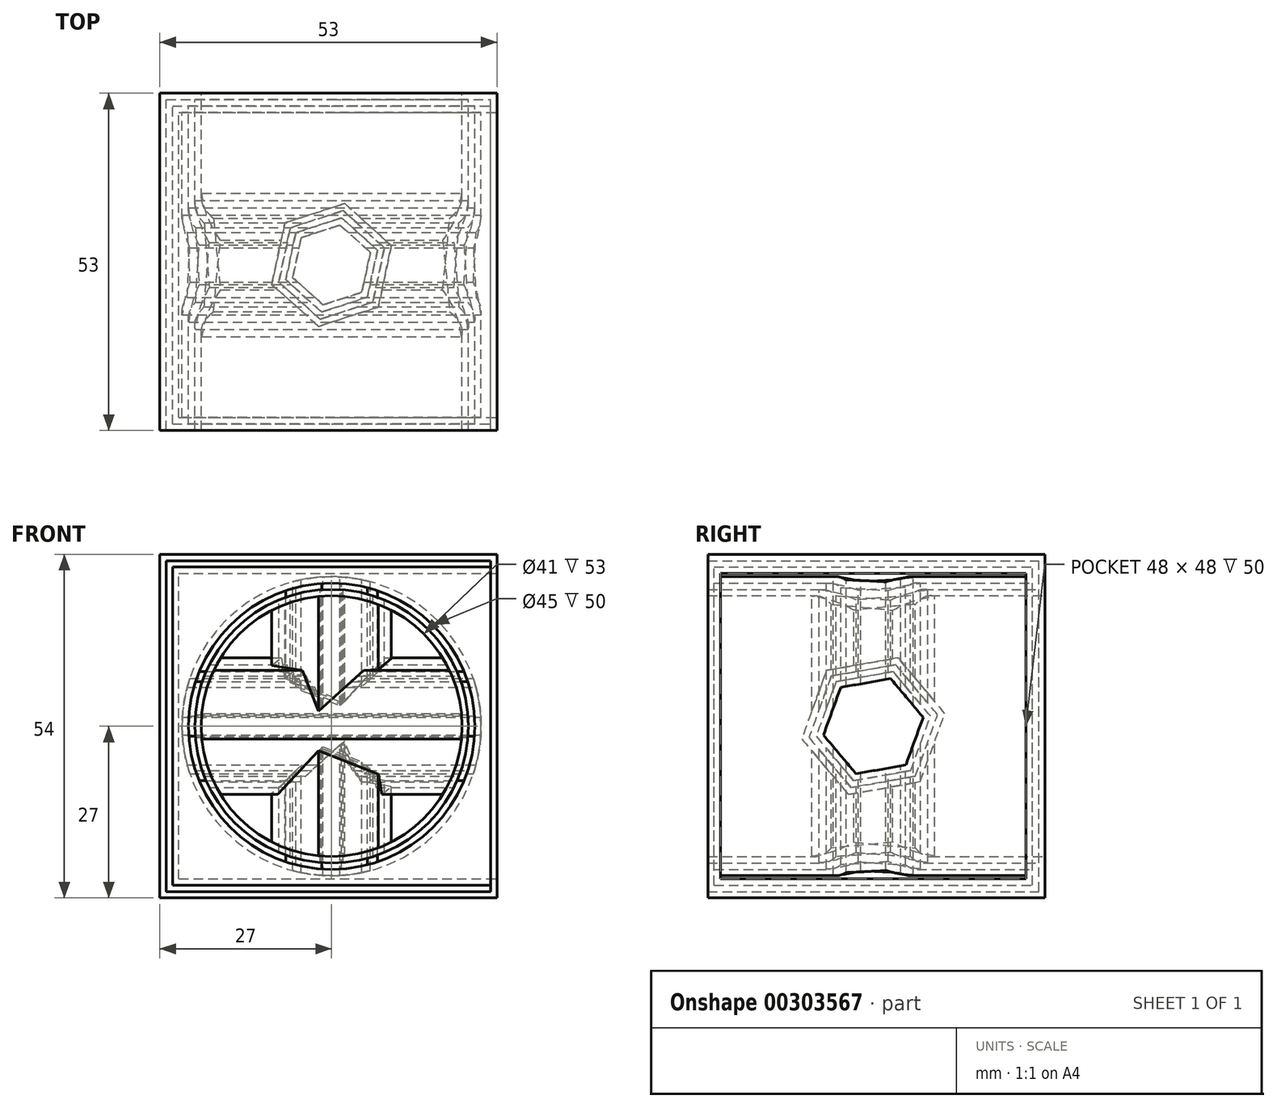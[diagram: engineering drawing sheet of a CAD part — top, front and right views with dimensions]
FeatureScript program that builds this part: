
annotation { "Feature Type Name" : "Feature", "Feature Type Description" : "" }
export const myFeature = defineFeature(function(context is Context, id is Id, definition is map)
    precondition{}
    {
        {
            var Q0;
            Q0=qCreatedBy(makeId("Front.planeOp"),FACE);
            var sketch = newSketch(context, id + "F0", { "sketchPlane" : qUnion([Q0])});
            skLineSegment(sketch, "E0.bottom", {"start": v(0, 0) * mm, "end": v(50, 0) * mm});
            skLineSegment(sketch, "E0.top", {"start": v(0, 50) * mm, "end": v(50, 50) * mm});
            skLineSegment(sketch, "E0.left", {"start": v(0, 0) * mm, "end": v(0, 50) * mm});
            skLineSegment(sketch, "E0.right", {"start": v(50, 0) * mm, "end": v(50, 50) * mm});
            skCircle(sketch, "E1", {"center": v(25, 25) * mm, "radius": 22.5 * mm});
            skLineSegment(sketch, "E2", {"start": v(0, 50) * mm, "end": v(50, 0) * mm, "construction": true});
            skLineSegment(sketch, "E3", {"start": v(50, 50) * mm, "end": v(0, 0) * mm, "construction": true});
            skSolve(sketch);
        }
        {
            var Q0;
            {var subQ0=sQuery(id+"F0.wireOp",EDGE,"E0.left");var subQ1=sQuery(id+"F0.wireOp",EDGE,"E0.bottom");var subQ2=makeQuery(id+"F0.imprint","INTERSECT",VERTEX,{"derivedFrom":[subQ1,subQ0]});Q0=makeQuery(id+"F0.imprint","IMPRINT",FACE,{"disambiguationData":[TD([[makeQuery(id+"F0.imprint","IMPRINT",EDGE,{"disambiguationData":[TD([[subQ2,-1.0]])],"derivedFrom":subQ1}),1.0]])]});}
            var Q1;
            {var subQ0=sQuery(id+"F0.wireOp",EDGE,"E0.right");var subQ1=sQuery(id+"F0.wireOp",EDGE,"E0.bottom");var subQ2=makeQuery(id+"F0.imprint","INTERSECT",VERTEX,{"derivedFrom":[subQ1,subQ0]});Q1=makeQuery(id+"F0.imprint","IMPRINT",FACE,{"disambiguationData":[TD([[makeQuery(id+"F0.imprint","IMPRINT",EDGE,{"disambiguationData":[TD([[subQ2,1.0]])],"derivedFrom":subQ1}),1.0]])]});}
            var Q2;
            {var subQ0=sQuery(id+"F0.wireOp",EDGE,"E0.left");var subQ1=sQuery(id+"F0.wireOp",EDGE,"E0.top");var subQ2=makeQuery(id+"F0.imprint","INTERSECT",VERTEX,{"derivedFrom":[subQ1,subQ0]});Q2=makeQuery(id+"F0.imprint","IMPRINT",FACE,{"disambiguationData":[TD([[makeQuery(id+"F0.imprint","IMPRINT",EDGE,{"disambiguationData":[TD([[subQ2,-1.0]])],"derivedFrom":subQ1}),-1.0]])]});}
            var Q3;
            {var subQ0=sQuery(id+"F0.wireOp",EDGE,"E0.right");var subQ1=sQuery(id+"F0.wireOp",EDGE,"E0.top");var subQ2=makeQuery(id+"F0.imprint","INTERSECT",VERTEX,{"derivedFrom":[subQ1,subQ0]});Q3=makeQuery(id+"F0.imprint","IMPRINT",FACE,{"disambiguationData":[TD([[makeQuery(id+"F0.imprint","IMPRINT",EDGE,{"disambiguationData":[TD([[subQ2,1.0]])],"derivedFrom":subQ1}),-1.0]])]});}
            extrude(context, id + "F1", {"entities" : qUnion([Q0, Q1, Q2, Q3]), "depth" : 50 * mm});
        }
        {
            var Q0;
            Q0=makeQuery(id+"F1.opExtrude","SWEPT_FACE",FACE,{"disambiguationData":[OSD([sQuery(id+"F0.wireOp",EDGE,"E0.top")])]});
            var sketch = newSketch(context, id + "F2", { "sketchPlane" : qUnion([Q0])});
            skCircle(sketch, "E4.cCircle", {"center": v(25, -25) * mm, "radius": 6.56 * mm, "construction": true});
            skLineSegment(sketch, "E4.0", {"start": v(26.57, -17.6) * mm, "end": v(32.2, -22.66) * mm});
            skLineSegment(sketch, "E4.1", {"start": v(32.2, -22.66) * mm, "end": v(30.63, -30.06) * mm});
            skLineSegment(sketch, "E4.2", {"start": v(30.63, -30.06) * mm, "end": v(23.43, -32.4) * mm});
            skLineSegment(sketch, "E4.3", {"start": v(23.43, -32.4) * mm, "end": v(17.8, -27.34) * mm});
            skLineSegment(sketch, "E4.4", {"start": v(17.8, -27.34) * mm, "end": v(19.37, -19.94) * mm});
            skLineSegment(sketch, "E4.5", {"start": v(19.37, -19.94) * mm, "end": v(26.57, -17.6) * mm});
            skPoint(sketch, "E4.0.midPoint", {"position": v(29.39, -20.13) * mm});
            skSolve(sketch);
        }
        {
            var Q0;
            Q0 = qSketchRegion(id + "F2", true);
            extrude(context, id + "F3", {"entities" : qUnion([Q0]), "operationType" : NewBodyOperationType.ADD, "oppositeDirection" : true, "depth" : 50 * mm});
        }
        {
            var Q0;
            Q0=makeQuery(id+"F1.opExtrude","SWEPT_FACE",FACE,{"disambiguationData":[OSD([sQuery(id+"F0.wireOp",EDGE,"E0.right")])]});
            var sketch = newSketch(context, id + "F4", { "sketchPlane" : qUnion([Q0])});
            skCircle(sketch, "E5.cCircle", {"center": v(-25, 25) * mm, "radius": 7.9 * mm, "construction": true});
            skLineSegment(sketch, "E5.0", {"start": v(-21.89, 33.57) * mm, "end": v(-16.03, 26.59) * mm});
            skLineSegment(sketch, "E5.1", {"start": v(-16.03, 26.59) * mm, "end": v(-19.14, 18.02) * mm});
            skLineSegment(sketch, "E5.2", {"start": v(-19.14, 18.02) * mm, "end": v(-28.11, 16.43) * mm});
            skLineSegment(sketch, "E5.3", {"start": v(-28.11, 16.43) * mm, "end": v(-33.97, 23.41) * mm});
            skLineSegment(sketch, "E5.4", {"start": v(-33.97, 23.41) * mm, "end": v(-30.86, 31.98) * mm});
            skLineSegment(sketch, "E5.5", {"start": v(-30.86, 31.98) * mm, "end": v(-21.89, 33.57) * mm});
            skPoint(sketch, "E5.0.midPoint", {"position": v(-18.96, 30.08) * mm});
            skSolve(sketch);
        }
        {
            var Q0;
            Q0 = qSketchRegion(id + "F4", true);
            extrude(context, id + "F5", {"entities" : qUnion([Q0]), "operationType" : NewBodyOperationType.ADD, "oppositeDirection" : true, "depth" : 50 * mm});
        }
        {
            var Q0;
            Q0=makeQuery(id+"F1.opExtrude","SWEPT_FACE",FACE,{"disambiguationData":[OSD([sQuery(id+"F0.wireOp",EDGE,"E0.right")])]});
            shell(context, id + "F6", {"entities" : qUnion([Q0]), "thickness" : 1 * mm, "oppositeDirection" : true});
        }
        {
            var Q0;
            Q0=makeQuery(id+"F1.opExtrude","CAP_FACE",FACE,{"disambiguationData":[OSD([sQuery(id+"F0.wireOp",EDGE,"E0.bottom"),sQuery(id+"F0.wireOp",EDGE,"E0.top"),sQuery(id+"F0.wireOp",EDGE,"E0.left"),sQuery(id+"F0.wireOp",EDGE,"E0.right"),sQuery(id+"F0.wireOp",EDGE,"E1")])],"isStart":false});
            shell(context, id + "F7", {"entities" : qUnion([Q0]), "thickness" : 1 * mm, "oppositeDirection" : true});
        }
    });
